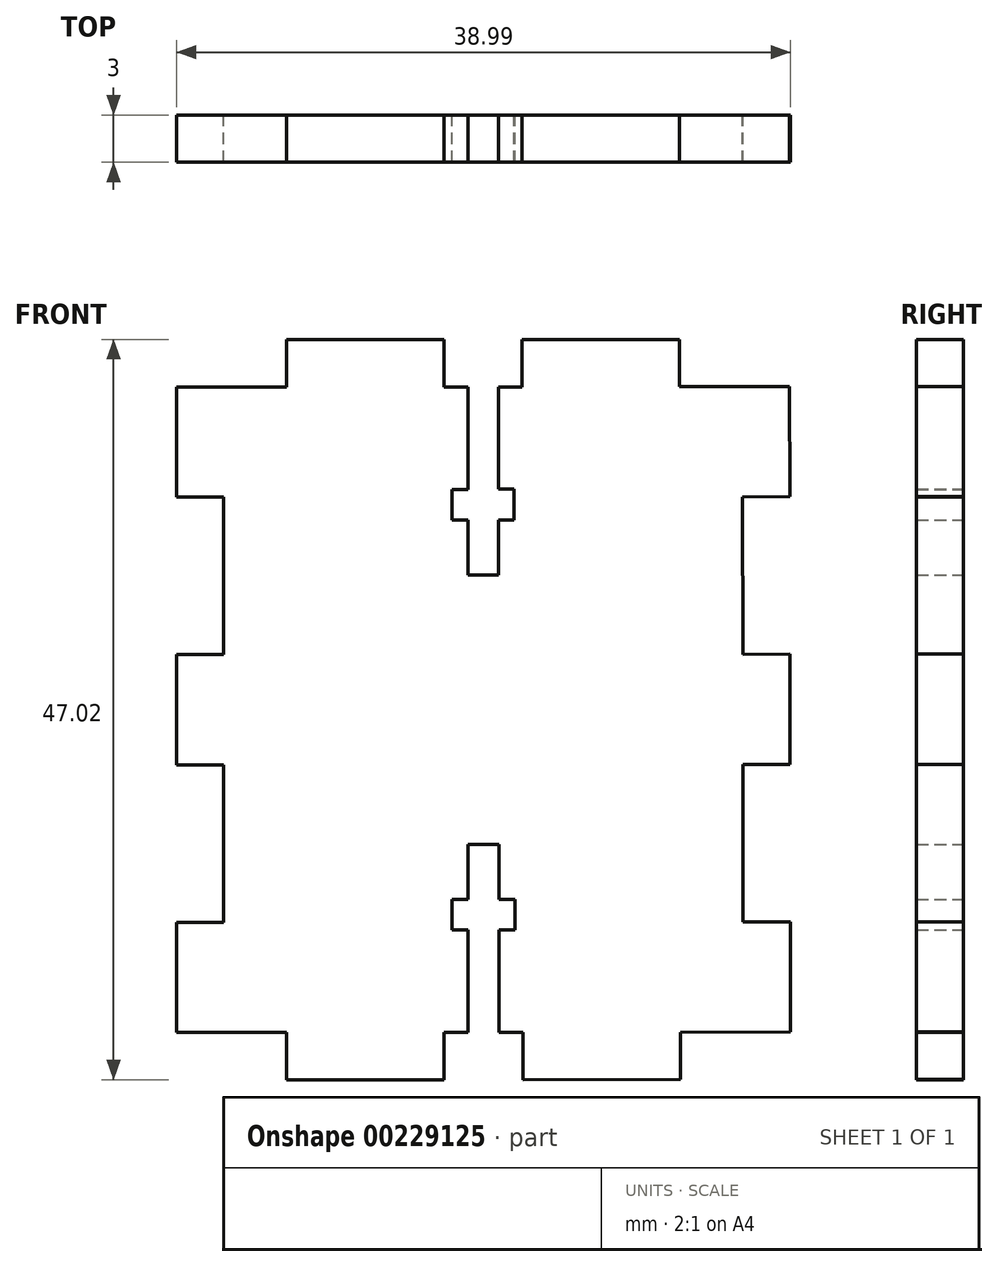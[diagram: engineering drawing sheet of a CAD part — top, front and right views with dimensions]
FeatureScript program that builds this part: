
annotation { "Feature Type Name" : "Feature", "Feature Type Description" : "" }
export const myFeature = defineFeature(function(context is Context, id is Id, definition is map)
    precondition{}
    {
        {
            var Q0;
            Q0=qCreatedBy(makeId("Front.planeOp"),FACE);
            var sketch = newSketch(context, id + "F0", { "sketchPlane" : qUnion([Q0])});
            skLineSegment(sketch, "E0", {"start": v(0, 24) * mm, "end": v(3, 24) * mm});
            skLineSegment(sketch, "E1", {"start": v(3, 24) * mm, "end": v(3, 34) * mm});
            skLineSegment(sketch, "E2", {"start": v(3, 34) * mm, "end": v(0, 34) * mm});
            skLineSegment(sketch, "E3", {"start": v(0, 34) * mm, "end": v(0, 41) * mm});
            skLineSegment(sketch, "E4", {"start": v(0, 41) * mm, "end": v(7, 41) * mm});
            skLineSegment(sketch, "E5", {"start": v(7, 41) * mm, "end": v(7, 44) * mm});
            skLineSegment(sketch, "E6", {"start": v(7, 44) * mm, "end": v(17, 44) * mm});
            skLineSegment(sketch, "E7", {"start": v(17, 44) * mm, "end": v(17, 41) * mm});
            skLineSegment(sketch, "E8", {"start": v(17, 41) * mm, "end": v(18.5, 41) * mm});
            skLineSegment(sketch, "E9", {"start": v(18.5, 41) * mm, "end": v(18.5, 34.5) * mm});
            skLineSegment(sketch, "E10", {"start": v(18.5, 32.55) * mm, "end": v(18.5, 29.05) * mm});
            skLineSegment(sketch, "E11", {"start": v(18.5, 29.05) * mm, "end": v(19.5, 29.05) * mm});
            skLineSegment(sketch, "E12", {"start": v(0, 20.5) * mm, "end": v(32.77, 20.5) * mm, "construction": true});
            skPoint(sketch, "E12.endSnap0", {"position": v(0, 20.5) * mm});
            skLineSegment(sketch, "E13", {"start": v(0, 24) * mm, "end": v(0, 20.5) * mm});
            skLineSegment(sketch, "E14.MirrorCS", {"start": v(18.5, 11.95) * mm, "end": v(19.5, 11.95) * mm});
            skLineSegment(sketch, "E15.MirrorCS", {"start": v(17, 0) * mm, "end": v(18.5, 0) * mm});
            skLineSegment(sketch, "E16.MirrorCS", {"start": v(18.5, 8.45) * mm, "end": v(18.5, 11.95) * mm});
            skLineSegment(sketch, "E17.MirrorCS", {"start": v(3, 17) * mm, "end": v(3, 7) * mm});
            skLineSegment(sketch, "E18.MirrorCS", {"start": v(3, 7) * mm, "end": v(0, 7) * mm});
            skLineSegment(sketch, "E19.MirrorCS", {"start": v(0, 0) * mm, "end": v(7, 0) * mm});
            skLineSegment(sketch, "E20.MirrorCS", {"start": v(7, 0) * mm, "end": v(7, -3) * mm});
            skLineSegment(sketch, "E21.MirrorCS", {"start": v(7, -3) * mm, "end": v(17, -3) * mm});
            skLineSegment(sketch, "E22.MirrorCS", {"start": v(18.5, 0) * mm, "end": v(18.5, 6.5) * mm});
            skLineSegment(sketch, "E23.MirrorCS", {"start": v(0, 7) * mm, "end": v(0, 0) * mm});
            skLineSegment(sketch, "E24.MirrorCS", {"start": v(0, 17) * mm, "end": v(0, 20.5) * mm});
            skLineSegment(sketch, "E25.MirrorCS", {"start": v(0, 17) * mm, "end": v(3, 17) * mm});
            skLineSegment(sketch, "E26.MirrorCS", {"start": v(17, -3) * mm, "end": v(17, 0) * mm});
            skLineSegment(sketch, "E27", {"start": v(19.46, 48.86) * mm, "end": v(19.5, -6.8) * mm, "construction": true});
            skLineSegment(sketch, "E28.MirrorCS", {"start": v(20.48, 11.95) * mm, "end": v(19.48, 11.95) * mm});
            skLineSegment(sketch, "E29.MirrorCS", {"start": v(22, -3) * mm, "end": v(22, 0) * mm});
            skLineSegment(sketch, "E30.MirrorCS", {"start": v(32, 0.02) * mm, "end": v(32, -2.98) * mm});
            skLineSegment(sketch, "E31.MirrorCS", {"start": v(35.98, 7.02) * mm, "end": v(38.98, 7.03) * mm});
            skLineSegment(sketch, "E32.MirrorCS", {"start": v(38.97, 17.03) * mm, "end": v(38.96, 20.53) * mm});
            skLineSegment(sketch, "E33.MirrorCS", {"start": v(22, 0) * mm, "end": v(20.5, 0) * mm});
            skLineSegment(sketch, "E34.MirrorCS", {"start": v(31.94, 41.02) * mm, "end": v(31.93, 44.02) * mm});
            skLineSegment(sketch, "E35.MirrorCS", {"start": v(20.45, 29.05) * mm, "end": v(19.45, 29.05) * mm});
            skLineSegment(sketch, "E36.MirrorCS", {"start": v(38.97, 17.03) * mm, "end": v(35.97, 17.02) * mm});
            skLineSegment(sketch, "E37.MirrorCS", {"start": v(38.96, 24.03) * mm, "end": v(38.96, 20.53) * mm});
            skLineSegment(sketch, "E38.MirrorCS", {"start": v(38.96, 24.03) * mm, "end": v(35.96, 24.02) * mm});
            skLineSegment(sketch, "E39.MirrorCS", {"start": v(21.93, 44) * mm, "end": v(21.94, 41) * mm});
            skLineSegment(sketch, "E40.MirrorCS", {"start": v(21.94, 41) * mm, "end": v(20.44, 41) * mm});
            skLineSegment(sketch, "E41.MirrorCS", {"start": v(35.95, 34.02) * mm, "end": v(38.95, 34.03) * mm});
            skPoint(sketch, "E42.MirrorP", {"position": v(38.96, 20.53) * mm});
            skLineSegment(sketch, "E43.MirrorCS", {"start": v(20.45, 32.55) * mm, "end": v(20.45, 29.05) * mm});
            skLineSegment(sketch, "E44.MirrorCS", {"start": v(20.5, 0) * mm, "end": v(20.48, 6.5) * mm});
            skLineSegment(sketch, "E45.MirrorCS", {"start": v(38.94, 41.03) * mm, "end": v(31.94, 41.02) * mm});
            skLineSegment(sketch, "E46.MirrorCS", {"start": v(35.97, 17.02) * mm, "end": v(35.98, 7.02) * mm});
            skLineSegment(sketch, "E47.MirrorCS", {"start": v(20.48, 8.45) * mm, "end": v(20.48, 11.95) * mm});
            skLineSegment(sketch, "E48.MirrorCS", {"start": v(38.95, 34.03) * mm, "end": v(38.94, 41.03) * mm});
            skLineSegment(sketch, "E49.MirrorCS", {"start": v(31.93, 44.02) * mm, "end": v(21.93, 44) * mm});
            skLineSegment(sketch, "E50.MirrorCS", {"start": v(38.96, 20.53) * mm, "end": v(6.2, 20.48) * mm, "construction": true});
            skLineSegment(sketch, "E51.MirrorCS", {"start": v(35.96, 24.02) * mm, "end": v(35.95, 34.02) * mm});
            skLineSegment(sketch, "E52.MirrorCS", {"start": v(39, 0.03) * mm, "end": v(32, 0.02) * mm});
            skLineSegment(sketch, "E53.MirrorCS", {"start": v(38.98, 7.03) * mm, "end": v(39, 0.03) * mm});
            skLineSegment(sketch, "E54.MirrorCS", {"start": v(20.44, 41) * mm, "end": v(20.45, 34.5) * mm});
            skLineSegment(sketch, "E55.MirrorCS", {"start": v(32, -2.98) * mm, "end": v(22, -3) * mm});
            skLineSegment(sketch, "E56", {"start": v(18.5, 34.5) * mm, "end": v(17.5, 34.5) * mm});
            skLineSegment(sketch, "E57", {"start": v(18.5, 32.55) * mm, "end": v(17.5, 32.55) * mm});
            skLineSegment(sketch, "E58", {"start": v(17.5, 34.5) * mm, "end": v(17.5, 32.55) * mm});
            skLineSegment(sketch, "E59", {"start": v(20.45, 32.55) * mm, "end": v(21.45, 32.56) * mm});
            skLineSegment(sketch, "E60", {"start": v(20.45, 34.5) * mm, "end": v(21.45, 34.5) * mm});
            skLineSegment(sketch, "E61", {"start": v(21.45, 34.5) * mm, "end": v(21.45, 32.56) * mm});
            skLineSegment(sketch, "E62", {"start": v(18.5, 8.45) * mm, "end": v(17.5, 8.45) * mm});
            skLineSegment(sketch, "E63", {"start": v(20.48, 8.45) * mm, "end": v(21.48, 8.45) * mm});
            skLineSegment(sketch, "E64", {"start": v(20.48, 6.5) * mm, "end": v(21.48, 6.5) * mm});
            skLineSegment(sketch, "E65", {"start": v(18.5, 6.5) * mm, "end": v(17.5, 6.5) * mm});
            skLineSegment(sketch, "E66", {"start": v(17.5, 8.45) * mm, "end": v(17.5, 6.5) * mm});
            skLineSegment(sketch, "E67", {"start": v(21.48, 8.45) * mm, "end": v(21.48, 6.5) * mm});
            skSolve(sketch);
        }
        {
            var Q0;
            Q0 = qSketchRegion(id + "F0", true);
            extrude(context, id + "F1", {"entities" : qUnion([Q0]), "depth" : 3 * mm});
        }
    });
